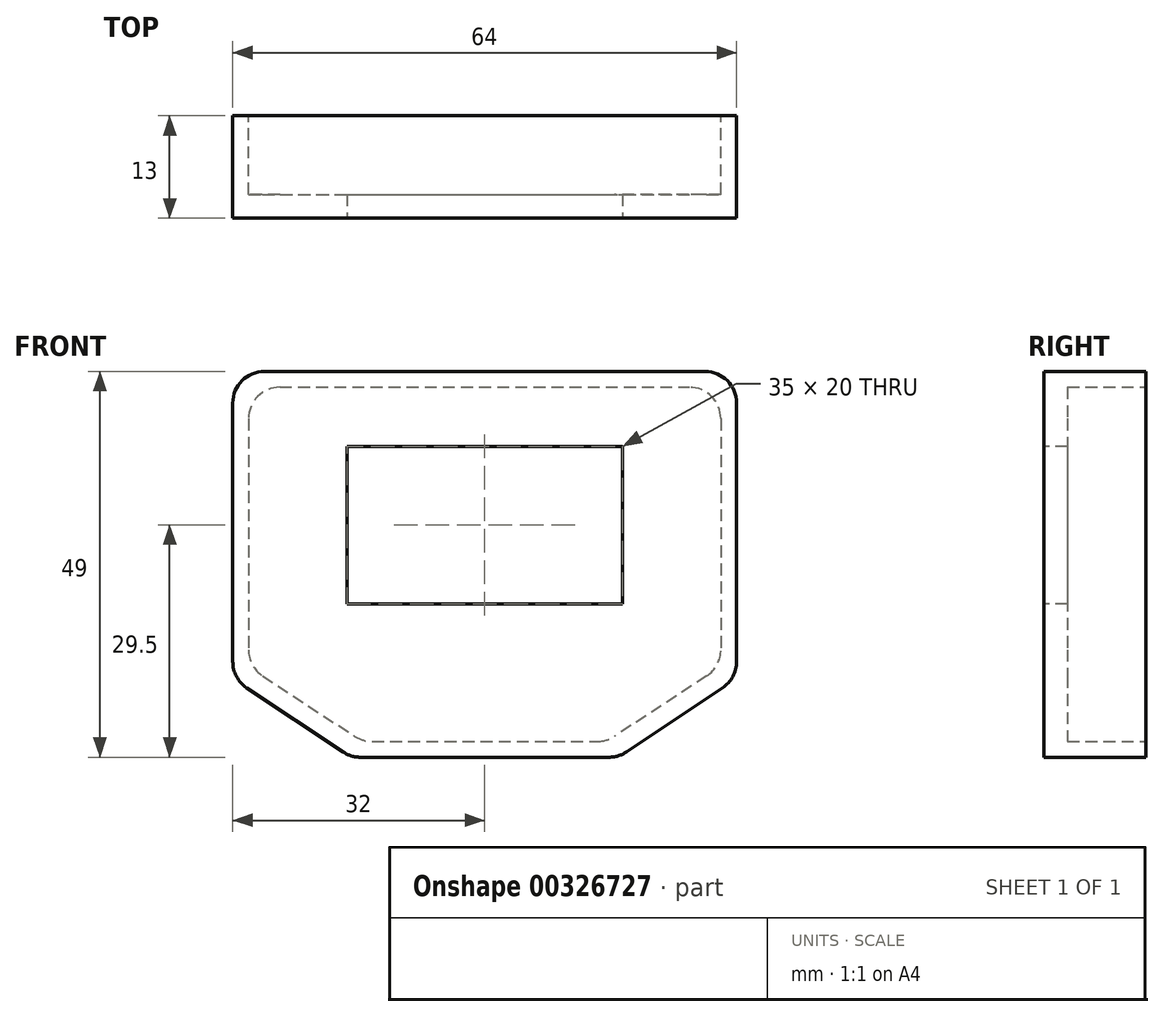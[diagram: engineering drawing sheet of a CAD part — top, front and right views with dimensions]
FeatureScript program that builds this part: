
annotation { "Feature Type Name" : "Feature", "Feature Type Description" : "" }
export const myFeature = defineFeature(function(context is Context, id is Id, definition is map)
    precondition{}
    {
        {
            var Q0;
            Q0=qCreatedBy(makeId("Front.planeOp"),FACE);
            var sketch = newSketch(context, id + "F0", { "sketchPlane" : qUnion([Q0])});
            skLineSegment(sketch, "E0.bottom", {"start": v(0, 0) * mm, "end": v(64, 0) * mm});
            skLineSegment(sketch, "E1", {"start": v(0, 0) * mm, "end": v(0, -2) * mm});
            skLineSegment(sketch, "E2", {"start": v(0, -2) * mm, "end": v(2, -2) * mm});
            skLineSegment(sketch, "E3.bottom", {"start": v(2, -2) * mm, "end": v(62, -2) * mm});
            skLineSegment(sketch, "E4", {"start": v(2, -2) * mm, "end": v(2, -37.5) * mm});
            skLineSegment(sketch, "E5", {"start": v(62, -2) * mm, "end": v(62, -37.5) * mm});
            skLineSegment(sketch, "E6", {"start": v(32, -49) * mm, "end": v(32, -47) * mm, "construction": true});
            skLineSegment(sketch, "E7", {"start": v(32, -47) * mm, "end": v(16.5, -47) * mm});
            skLineSegment(sketch, "E8", {"start": v(32, -47) * mm, "end": v(47.5, -47) * mm});
            skLineSegment(sketch, "E9", {"start": v(64, 0) * mm, "end": v(64, -39) * mm});
            skLineSegment(sketch, "E10", {"start": v(0, 0) * mm, "end": v(0, -39) * mm});
            skLineSegment(sketch, "E11", {"start": v(32, -49) * mm, "end": v(15, -49) * mm});
            skLineSegment(sketch, "E12", {"start": v(32, -49) * mm, "end": v(49, -49) * mm});
            skLineSegment(sketch, "E13", {"start": v(2, -37.5) * mm, "end": v(16.5, -47) * mm});
            skLineSegment(sketch, "E14", {"start": v(15, -49) * mm, "end": v(0, -39) * mm});
            skLineSegment(sketch, "E15", {"start": v(62, -37.5) * mm, "end": v(47.5, -47) * mm});
            skLineSegment(sketch, "E16", {"start": v(49, -49) * mm, "end": v(64, -39) * mm});
            skSolve(sketch);
        }
        {
            var Q0;
            Q0=makeQuery(id+"F0.imprint","IMPRINT",FACE,{"disambiguationData":[TD([[makeQuery(id+"F0.imprint","IMPRINT",EDGE,{"derivedFrom":sQuery(id+"F0.wireOp",EDGE,"E0.bottom")}),-1.0]])]});
            extrude(context, id + "F1", {"entities" : qUnion([Q0]), "depth" : 10 * mm});
        }
        {
            var Q0;
            Q0=makeQuery(id+"F1.opExtrude","CAP_FACE",FACE,{"disambiguationData":[OSD([sQuery(id+"F0.wireOp",EDGE,"E0.bottom"),sQuery(id+"F0.wireOp",EDGE,"E3.bottom"),sQuery(id+"F0.wireOp",EDGE,"E4"),sQuery(id+"F0.wireOp",EDGE,"E5"),sQuery(id+"F0.wireOp",EDGE,"E7"),sQuery(id+"F0.wireOp",EDGE,"E8"),sQuery(id+"F0.wireOp",EDGE,"ZbWCL8qp-J8rE-5joA-WxzC-bdhauH3AYqTg"),sQuery(id+"F0.wireOp",EDGE,"ljqWTU16-GMCM-zycx-PwWE-svwn7AJD2eyw"),sQuery(id+"F0.wireOp",EDGE,"E9"),sQuery(id+"F0.wireOp",EDGE,"E10"),sQuery(id+"F0.wireOp",EDGE,"E11"),sQuery(id+"F0.wireOp",EDGE,"E12"),sQuery(id+"F0.wireOp",EDGE,"MJg28nbz-v39h-hp56-AFMf-SzZ0Ew2wvrm0"),sQuery(id+"F0.wireOp",EDGE,"topSXZ4C-VmUy-RHna-zfik-yiPFlYJXgPlb")])],"isStart":false});
            var sketch = newSketch(context, id + "F2", { "sketchPlane" : qUnion([Q0])});
            skLineSegment(sketch, "E17", {"start": v(0, 0) * mm, "end": v(0, 0) * mm});
            skLineSegment(sketch, "E18", {"start": v(15, -49) * mm, "end": v(49, -49) * mm});
            skLineSegment(sketch, "E19", {"start": v(64, 0) * mm, "end": v(64, 0) * mm});
            skLineSegment(sketch, "E20", {"start": v(64, 0) * mm, "end": v(0, 0) * mm});
            skLineSegment(sketch, "E21", {"start": v(0, 0) * mm, "end": v(0, -39) * mm});
            skLineSegment(sketch, "E22", {"start": v(0, -39) * mm, "end": v(15, -49) * mm});
            skLineSegment(sketch, "E23", {"start": v(49, -49) * mm, "end": v(64, -39) * mm});
            skLineSegment(sketch, "E24", {"start": v(64, -39) * mm, "end": v(64, 0) * mm});
            skSolve(sketch);
        }
        {
            var Q0;
            Q0 = qSketchRegion(id + "F2", true);
            extrude(context, id + "F3", {"entities" : qUnion([Q0]), "operationType" : NewBodyOperationType.ADD, "depth" : 3 * mm});
        }
        {
            var Q0;
            Q0=makeQuery(id+"F3.opExtrude","CAP_FACE",FACE,{"disambiguationData":[OSD([sQuery(id+"F2.wireOp",EDGE,"E17"),sQuery(id+"F2.wireOp",EDGE,"4iCf0wS4-1aGP-d9Sk-ucEz-KT2urozeKg3Y"),sQuery(id+"F2.wireOp",EDGE,"E18"),sQuery(id+"F2.wireOp",EDGE,"jnfGQmym-1CfN-w9iP-vlof-awFA87Rw3nxD"),sQuery(id+"F2.wireOp",EDGE,"E19"),sQuery(id+"F2.wireOp",EDGE,"E20")])],"isStart":false});
            var sketch = newSketch(context, id + "F4", { "sketchPlane" : qUnion([Q0])});
            skLineSegment(sketch, "E25", {"start": v(0, 0) * mm, "end": v(0, -9.5) * mm, "construction": true});
            skLineSegment(sketch, "E26", {"start": v(0, -9.5) * mm, "end": v(14.5, -9.5) * mm, "construction": true});
            skLineSegment(sketch, "E27.bottom", {"start": v(14.5, -9.5) * mm, "end": v(49.5, -9.5) * mm});
            skLineSegment(sketch, "E27.top", {"start": v(14.5, -29.5) * mm, "end": v(49.5, -29.5) * mm});
            skLineSegment(sketch, "E27.left", {"start": v(14.5, -9.5) * mm, "end": v(14.5, -29.5) * mm});
            skLineSegment(sketch, "E27.right", {"start": v(49.5, -9.5) * mm, "end": v(49.5, -29.5) * mm});
            skSolve(sketch);
        }
        {
            var Q0;
            Q0=makeQuery(id+"F4.imprint","IMPRINT",FACE,{"disambiguationData":[TD([[makeQuery(id+"F4.imprint","IMPRINT",EDGE,{"derivedFrom":sQuery(id+"F4.wireOp",EDGE,"E27.bottom")}),-1.0]])]});
            extrude(context, id + "F5", {"entities" : qUnion([Q0]), "operationType" : NewBodyOperationType.REMOVE, "oppositeDirection" : true, "depth" : 25 * mm});
        }
        {
            var Q0;
            Q0=makeQuery(id+"F3.boolean.opBoolean","MERGE",EDGE,{"derivedFrom":[makeQuery(id+"F1.opExtrude","SWEPT_EDGE",EDGE,{"disambiguationData":[OSD([sQuery(id+"F0.wireOp",EDGE,"E0.bottom"),sQuery(id+"F0.wireOp",EDGE,"E9")])]}),makeQuery(id+"F3.opExtrude","SWEPT_EDGE",EDGE,{"disambiguationData":[OSD([sQuery(id+"F2.wireOp",EDGE,"E20"),sQuery(id+"F2.wireOp",EDGE,"E24")])]})]});
            fillet(context, id + "F6", {"entities" : qUnion([Q0]), "radius" : 4 * mm, "tangentPropagation" : true, "allowEdgeOverflow" : false});
        }
        {
            var Q0;
            Q0=makeQuery(id+"F3.boolean.opBoolean","MERGE",EDGE,{"derivedFrom":[makeQuery(id+"F1.opExtrude","SWEPT_EDGE",EDGE,{"disambiguationData":[OSD([sQuery(id+"F0.wireOp",EDGE,"E0.bottom"),sQuery(id+"F0.wireOp",EDGE,"E10")])]}),makeQuery(id+"F3.opExtrude","SWEPT_EDGE",EDGE,{"disambiguationData":[OSD([sQuery(id+"F2.wireOp",EDGE,"E20"),sQuery(id+"F2.wireOp",EDGE,"E21")])]})]});
            var Q1;
            Q1=makeQuery(id+"F3.boolean.opBoolean","MERGE",EDGE,{"derivedFrom":[makeQuery(id+"F1.opExtrude","SWEPT_EDGE",EDGE,{"disambiguationData":[OSD([sQuery(id+"F0.wireOp",EDGE,"E9"),sQuery(id+"F0.wireOp",EDGE,"E16")])]}),makeQuery(id+"F3.opExtrude","SWEPT_EDGE",EDGE,{"disambiguationData":[OSD([sQuery(id+"F2.wireOp",EDGE,"E23"),sQuery(id+"F2.wireOp",EDGE,"E24")])]})]});
            var Q2;
            Q2=makeQuery(id+"F3.boolean.opBoolean","MERGE",EDGE,{"derivedFrom":[makeQuery(id+"F1.opExtrude","SWEPT_EDGE",EDGE,{"disambiguationData":[OSD([sQuery(id+"F0.wireOp",EDGE,"E12"),sQuery(id+"F0.wireOp",EDGE,"E16")])]}),makeQuery(id+"F3.opExtrude","SWEPT_EDGE",EDGE,{"disambiguationData":[OSD([sQuery(id+"F2.wireOp",EDGE,"E18"),sQuery(id+"F2.wireOp",EDGE,"E23")])]})]});
            var Q3;
            Q3=makeQuery(id+"F3.boolean.opBoolean","MERGE",EDGE,{"derivedFrom":[makeQuery(id+"F1.opExtrude","SWEPT_EDGE",EDGE,{"disambiguationData":[OSD([sQuery(id+"F0.wireOp",EDGE,"E11"),sQuery(id+"F0.wireOp",EDGE,"E14")])]}),makeQuery(id+"F3.opExtrude","SWEPT_EDGE",EDGE,{"disambiguationData":[OSD([sQuery(id+"F2.wireOp",EDGE,"E18"),sQuery(id+"F2.wireOp",EDGE,"E22")])]})]});
            var Q4;
            Q4=makeQuery(id+"F3.boolean.opBoolean","MERGE",EDGE,{"derivedFrom":[makeQuery(id+"F1.opExtrude","SWEPT_EDGE",EDGE,{"disambiguationData":[OSD([sQuery(id+"F0.wireOp",EDGE,"E10"),sQuery(id+"F0.wireOp",EDGE,"E14")])]}),makeQuery(id+"F3.opExtrude","SWEPT_EDGE",EDGE,{"disambiguationData":[OSD([sQuery(id+"F2.wireOp",EDGE,"E21"),sQuery(id+"F2.wireOp",EDGE,"E22")])]})]});
            fillet(context, id + "F7", {"entities" : qUnion([Q0, Q1, Q2, Q3, Q4]), "radius" : 4 * mm, "tangentPropagation" : true, "allowEdgeOverflow" : false});
        }
        {
            var Q0;
            Q0=makeQuery(id+"F1.opExtrude","SWEPT_EDGE",EDGE,{"disambiguationData":[OSD([sQuery(id+"F0.wireOp",EDGE,"E3.bottom"),sQuery(id+"F0.wireOp",EDGE,"E4")])]});
            var Q1;
            Q1=makeQuery(id+"F1.opExtrude","SWEPT_EDGE",EDGE,{"disambiguationData":[OSD([sQuery(id+"F0.wireOp",EDGE,"E4"),sQuery(id+"F0.wireOp",EDGE,"E13")])]});
            var Q2;
            Q2=makeQuery(id+"F1.opExtrude","SWEPT_EDGE",EDGE,{"disambiguationData":[OSD([sQuery(id+"F0.wireOp",EDGE,"E3.bottom"),sQuery(id+"F0.wireOp",EDGE,"E5")])]});
            var Q3;
            Q3=makeQuery(id+"F1.opExtrude","SWEPT_EDGE",EDGE,{"disambiguationData":[OSD([sQuery(id+"F0.wireOp",EDGE,"E5"),sQuery(id+"F0.wireOp",EDGE,"E15")])]});
            var Q4;
            Q4=makeQuery(id+"F1.opExtrude","SWEPT_EDGE",EDGE,{"disambiguationData":[OSD([sQuery(id+"F0.wireOp",EDGE,"E8"),sQuery(id+"F0.wireOp",EDGE,"E15")])]});
            var Q5;
            Q5=makeQuery(id+"F1.opExtrude","SWEPT_EDGE",EDGE,{"disambiguationData":[OSD([sQuery(id+"F0.wireOp",EDGE,"E7"),sQuery(id+"F0.wireOp",EDGE,"E13")])]});
            fillet(context, id + "F8", {"entities" : qUnion([Q0, Q1, Q2, Q3, Q4, Q5]), "radius" : 4 * mm, "tangentPropagation" : true, "allowEdgeOverflow" : false});
        }
    });
